# Revit family: Urinal-Rear_Spud-Sloan-SU-7419_Series
name_source: partatom
category: Plumbing Fixtures
revit_build: Autodesk Revit 2014 (Build: 20130308_1515(x64)
units: mm (PartAtom-declared; Revit-internal decimal feet)

## types (2) — shared parameters
ADA Compliant = Yes
Assembly Code = D2010210
CW Connection = No
CWFU = 5
Default Elevation = 24"
Fixture Color = White
Flush Volumes and Flow Rates = 0.125 to 1.0 gpf
HW Connection = No
Height = 23 1/8"
Length = 14 3/16"
Manufacturer = Sloan
Material = Vitreous China-Sloan-White
Mounting = Wall Hung
Price = Prices may vary. Please consult Sloan Rep for most up-to-date price list.
Revised Date = 5/4/2018
Spud Location = Rear Spud
URL = www.sloan.com
Vent Connection = No
WFU = 5
Warranty = 3 Year (Limited)
Waste Connection = Yes
Waste Connection Diameter = 2"
Waste Connection Radius = 1"
zero-valued in all types: HWFU

## per-type parameters (varying)
| type | Description | Flush Choice | Order Code |
| SU-7419 | Small Designer Urinal, Rear Spud, 0.125 to 1.0 gpf | Single Flush | 1107419 |
| SU-7419-STG | Small Designer Urinal with SloanTec Glaze, Rear Spud, 0.125 to 1.0 gpf | Waterfree | 1177419 |

note: column(s) folded — value = type name in every type: Model

## geometry (parser evidence)
native form markers: Sweep x3
no freeform markers — native parametric forms only
